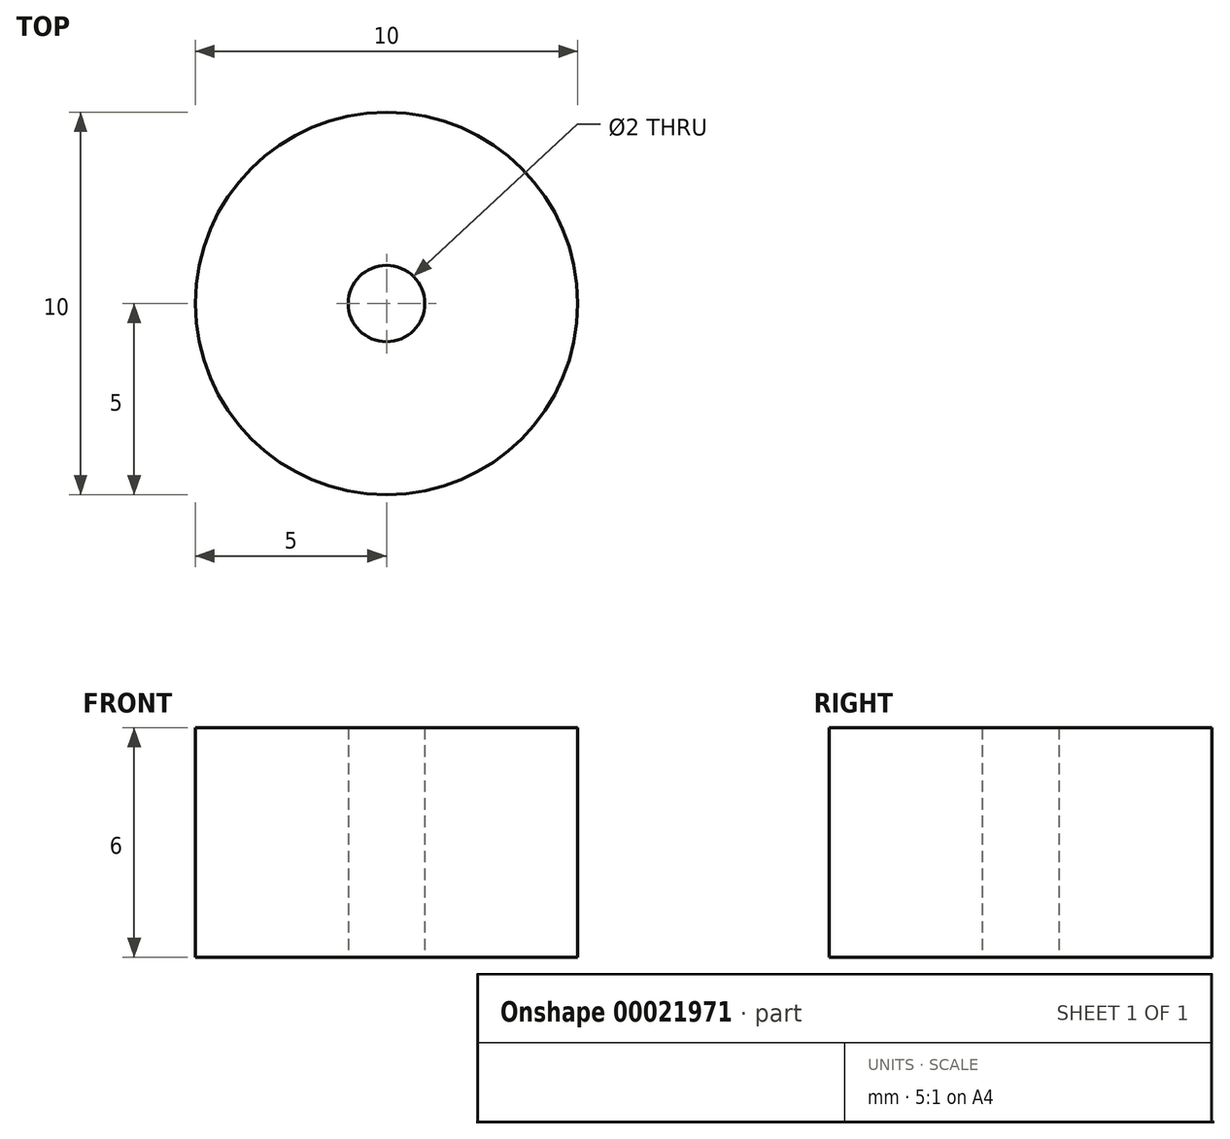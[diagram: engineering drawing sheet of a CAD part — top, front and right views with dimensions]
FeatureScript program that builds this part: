
annotation { "Feature Type Name" : "Feature", "Feature Type Description" : "" }
export const myFeature = defineFeature(function(context is Context, id is Id, definition is map)
    precondition{}
    {
        {
            var Q0;
            Q0=qCreatedBy(makeId("Top.planeOp"),FACE);
            var sketch = newSketch(context, id + "F0", { "sketchPlane" : qUnion([Q0])});
            skCircle(sketch, "E0", {"center": v(0, 0) * mm, "radius": 5 * mm});
            skCircle(sketch, "E1", {"center": v(0, 0) * mm, "radius": 1 * mm});
            skSolve(sketch);
        }
        {
            var Q0;
            Q0=makeQuery(id+"F0.imprint","IMPRINT",FACE,{"disambiguationData":[TD([[makeQuery(id+"F0.imprint","IMPRINT",EDGE,{"derivedFrom":sQuery(id+"F0.wireOp",EDGE,"E0")}),1.0]])]});
            extrude(context, id + "F1", {"entities" : qUnion([Q0]), "endBound" : BoundingType.SYMMETRIC, "depth" : 6 * mm});
        }
    });
